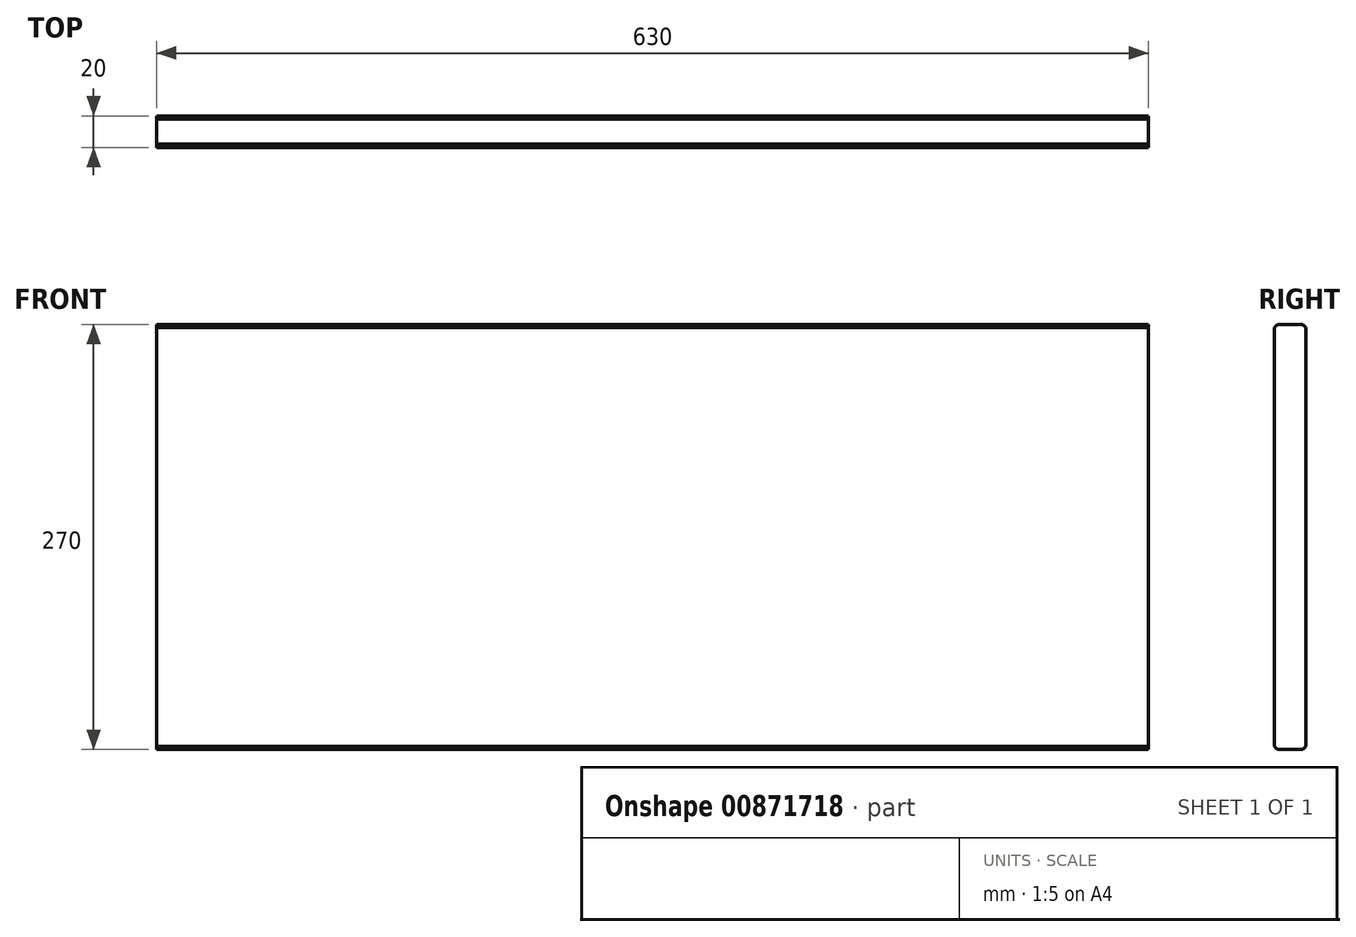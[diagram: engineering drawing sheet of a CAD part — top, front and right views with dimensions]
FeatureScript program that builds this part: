
annotation { "Feature Type Name" : "Feature", "Feature Type Description" : "" }
export const myFeature = defineFeature(function(context is Context, id is Id, definition is map)
    precondition{}
    {
        {
            var Q0;
            Q0=qCreatedBy(makeId("Front.planeOp"),FACE);
            var sketch = newSketch(context, id + "F0", { "sketchPlane" : qUnion([Q0])});
            skLineSegment(sketch, "E0.bottom", {"start": v(0, 0) * mm, "end": v(630, 0) * mm});
            skLineSegment(sketch, "E0.top", {"start": v(0, 270) * mm, "end": v(630, 270) * mm});
            skLineSegment(sketch, "E0.left", {"start": v(0, 0) * mm, "end": v(0, 270) * mm});
            skLineSegment(sketch, "E0.right", {"start": v(630, 0) * mm, "end": v(630, 270) * mm});
            skSolve(sketch);
        }
        {
            var Q0;
            Q0=makeQuery(id+"F0.imprint","IMPRINT",FACE,{"disambiguationData":[TD([[makeQuery(id+"F0.imprint","IMPRINT",EDGE,{"derivedFrom":sQuery(id+"F0.wireOp",EDGE,"E0.bottom")}),1.0]])]});
            extrude(context, id + "F1", {"entities" : qUnion([Q0]), "depth" : 20 * mm, "offsetDistance" : 25 * mm});
        }
        {
            var Q0;
            Q0=makeQuery(id+"F1.opExtrude","CAP_EDGE",EDGE,{"disambiguationData":[OSD([sQuery(id+"F0.wireOp",EDGE,"E0.bottom")])],"isStart":true});
            var Q1;
            Q1=makeQuery(id+"F1.opExtrude","CAP_EDGE",EDGE,{"disambiguationData":[OSD([sQuery(id+"F0.wireOp",EDGE,"E0.bottom")])],"isStart":false});
            var Q2;
            Q2=makeQuery(id+"F1.opExtrude","CAP_EDGE",EDGE,{"disambiguationData":[OSD([sQuery(id+"F0.wireOp",EDGE,"E0.top")])],"isStart":true});
            var Q3;
            Q3=makeQuery(id+"F1.opExtrude","CAP_EDGE",EDGE,{"disambiguationData":[OSD([sQuery(id+"F0.wireOp",EDGE,"E0.top")])],"isStart":false});
            chamfer(context, id + "F2", {"entities" : qUnion([Q0, Q1, Q2, Q3]), "width" : 2 * mm, "tangentPropagation" : true});
        }
    });
